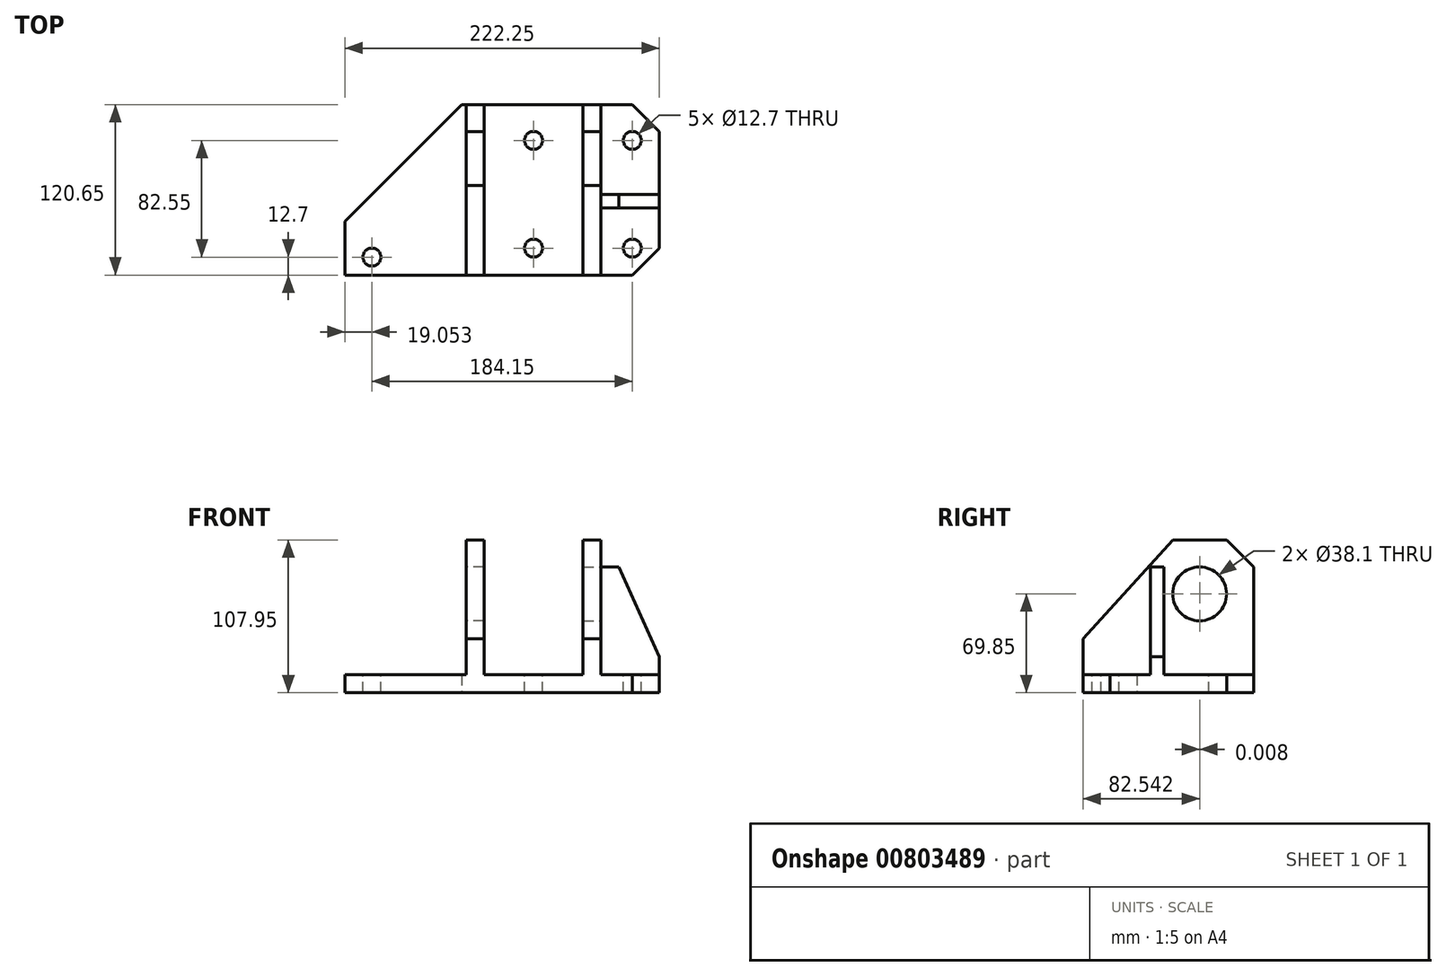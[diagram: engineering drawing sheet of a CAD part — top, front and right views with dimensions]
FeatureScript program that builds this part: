
annotation { "Feature Type Name" : "Feature", "Feature Type Description" : "" }
export const myFeature = defineFeature(function(context is Context, id is Id, definition is map)
    precondition{}
    {
        {
            var Q0;
            Q0=qCreatedBy(makeId("Top.planeOp"),FACE);
            var sketch = newSketch(context, id + "F0", { "sketchPlane" : qUnion([Q0])});
            skLineSegment(sketch, "E0", {"start": v(-62.09, -1.4) * mm, "end": v(-62.09, -39.5) * mm});
            skLineSegment(sketch, "E1", {"start": v(-62.09, -39.5) * mm, "end": v(141.11, -39.5) * mm});
            skLineSegment(sketch, "E2", {"start": v(160.16, -20.46) * mm, "end": v(160.16, 81.14) * mm});
            skLineSegment(sketch, "E3", {"start": v(160.16, -20.46) * mm, "end": v(141.11, -39.5) * mm});
            skLineSegment(sketch, "E4", {"start": v(160.16, 81.14) * mm, "end": v(71.26, 81.14) * mm});
            skLineSegment(sketch, "E5", {"start": v(71.26, 81.14) * mm, "end": v(36.34, 81.14) * mm});
            skLineSegment(sketch, "E6", {"start": v(36.34, 81.14) * mm, "end": v(20.46, 81.14) * mm});
            skLineSegment(sketch, "E7", {"start": v(20.46, 81.14) * mm, "end": v(-62.09, -1.4) * mm});
            skSolve(sketch);
        }
        {
            var Q0;
            Q0 = qSketchRegion(id + "F0", true);
            extrude(context, id + "F1", {"entities" : qUnion([Q0]), "depth" : 12.7 * mm, "offsetDistance" : 25.4 * mm});
        }
        {
            var Q0;
            Q0=makeQuery(id+"F1.opExtrude","CAP_FACE",FACE,{"disambiguationData":[OSD([sQuery(id+"F0.wireOp",EDGE,"E0"),sQuery(id+"F0.wireOp",EDGE,"E1"),sQuery(id+"F0.wireOp",EDGE,"E2"),sQuery(id+"F0.wireOp",EDGE,"E3"),sQuery(id+"F0.wireOp",EDGE,"E4"),sQuery(id+"F0.wireOp",EDGE,"E5"),sQuery(id+"F0.wireOp",EDGE,"E6"),sQuery(id+"F0.wireOp",EDGE,"E7")])],"isStart":false});
            var sketch = newSketch(context, id + "F2", { "sketchPlane" : qUnion([Q0])});
            skLineSegment(sketch, "E8", {"start": v(160.16, 81.14) * mm, "end": v(160.16, 62.1) * mm});
            skLineSegment(sketch, "E9", {"start": v(160.16, 81.14) * mm, "end": v(141.11, 81.14) * mm});
            skLineSegment(sketch, "E10", {"start": v(141.11, 81.14) * mm, "end": v(160.16, 62.1) * mm});
            skSolve(sketch);
        }
        {
            var Q0;
            Q0 = qSketchRegion(id + "F2", true);
            extrude(context, id + "F3", {"entities" : qUnion([Q0]), "operationType" : NewBodyOperationType.REMOVE, "oppositeDirection" : true, "depth" : 25.4 * mm, "offsetDistance" : 25.4 * mm});
        }
        {
            var Q0;
            Q0=makeQuery(id+"F1.opExtrude","CAP_FACE",FACE,{"disambiguationData":[OSD([sQuery(id+"F0.wireOp",EDGE,"E0"),sQuery(id+"F0.wireOp",EDGE,"E1"),sQuery(id+"F0.wireOp",EDGE,"E2"),sQuery(id+"F0.wireOp",EDGE,"E3"),sQuery(id+"F0.wireOp",EDGE,"E4"),sQuery(id+"F0.wireOp",EDGE,"E5"),sQuery(id+"F0.wireOp",EDGE,"E6"),sQuery(id+"F0.wireOp",EDGE,"E7")])],"isStart":false});
            var sketch = newSketch(context, id + "F4", { "sketchPlane" : qUnion([Q0])});
            skLineSegment(sketch, "E11", {"start": v(20.46, 81.14) * mm, "end": v(23.64, 81.14) * mm});
            skLineSegment(sketch, "E12", {"start": v(23.64, 81.14) * mm, "end": v(36.34, 81.14) * mm});
            skLineSegment(sketch, "E13", {"start": v(36.34, 81.14) * mm, "end": v(36.34, -39.5) * mm});
            skLineSegment(sketch, "E14", {"start": v(23.64, 81.14) * mm, "end": v(23.64, -39.5) * mm});
            skLineSegment(sketch, "E15", {"start": v(36.34, 81.14) * mm, "end": v(106.19, 81.14) * mm});
            skLineSegment(sketch, "E16", {"start": v(106.19, 81.14) * mm, "end": v(106.19, -39.5) * mm});
            skLineSegment(sketch, "E17", {"start": v(106.19, -39.5) * mm, "end": v(106.19, 81.14) * mm});
            skLineSegment(sketch, "E18", {"start": v(106.19, 81.14) * mm, "end": v(118.89, 81.14) * mm});
            skLineSegment(sketch, "E19", {"start": v(118.89, 81.14) * mm, "end": v(118.89, -39.5) * mm});
            skLineSegment(sketch, "E20", {"start": v(118.89, -39.5) * mm, "end": v(106.19, -39.5) * mm});
            skLineSegment(sketch, "E21", {"start": v(36.34, -39.5) * mm, "end": v(23.64, -39.5) * mm});
            skSolve(sketch);
        }
        {
            var Q0;
            Q0 = qSketchRegion(id + "F4", true);
            extrude(context, id + "F5", {"entities" : qUnion([Q0]), "operationType" : NewBodyOperationType.ADD, "depth" : 95.25 * mm, "offsetDistance" : 25.4 * mm});
        }
        {
            var Q0;
            Q0=makeQuery(id+"F5.opExtrude","SWEPT_FACE",FACE,{"disambiguationData":[OSD([sQuery(id+"F4.wireOp",EDGE,"E14")])]});
            var sketch = newSketch(context, id + "F6", { "sketchPlane" : qUnion([Q0])});
            skLineSegment(sketch, "E22", {"start": v(-81.14, 107.95) * mm, "end": v(-62.1, 107.95) * mm});
            skLineSegment(sketch, "E23", {"start": v(-81.14, 107.95) * mm, "end": v(-81.14, 88.9) * mm});
            skLineSegment(sketch, "E24", {"start": v(-81.14, 88.9) * mm, "end": v(-62.1, 107.95) * mm});
            skSolve(sketch);
        }
        {
            var Q0;
            Q0 = qSketchRegion(id + "F6", true);
            extrude(context, id + "F7", {"entities" : qUnion([Q0]), "operationType" : NewBodyOperationType.REMOVE, "oppositeDirection" : true, "depth" : 25.4 * mm, "offsetDistance" : 25.4 * mm});
        }
        {
            var Q0;
            Q0=makeQuery(id+"F5.opExtrude","SWEPT_FACE",FACE,{"disambiguationData":[OSD([sQuery(id+"F4.wireOp",EDGE,"E14")])]});
            var sketch = newSketch(context, id + "F8", { "sketchPlane" : qUnion([Q0])});
            skLineSegment(sketch, "E25", {"start": v(-62.1, 107.95) * mm, "end": v(-24, 107.95) * mm});
            skLineSegment(sketch, "E26", {"start": v(39.5, 12.7) * mm, "end": v(39.5, 38.1) * mm});
            skLineSegment(sketch, "E27", {"start": v(39.5, 38.1) * mm, "end": v(-24, 107.95) * mm});
            skSolve(sketch);
        }
        {
            var Q0;
            Q0 = qSketchRegion(id + "F8", true);
            var Q1;
            {var subQ0=sQuery(id+"F8.wireOp",EDGE,"E27");Q1=makeQuery(id+"F8.imprint","IMPRINT",FACE,{"disambiguationData":[TD([[makeQuery(id+"F8.imprint","IMPRINT",EDGE,{"derivedFrom":subQ0}),-1.0]])]});}
            extrude(context, id + "F9", {"entities" : qUnion([Q0, Q1]), "operationType" : NewBodyOperationType.REMOVE, "oppositeDirection" : true, "depth" : 25.4 * mm, "offsetDistance" : 25.4 * mm});
        }
        {
            var Q0;
            Q0=makeQuery(id+"F5.opExtrude","SWEPT_FACE",FACE,{"disambiguationData":[OSD([sQuery(id+"F4.wireOp",EDGE,"E19")])]});
            var sketch = newSketch(context, id + "F10", { "sketchPlane" : qUnion([Q0])});
            skLineSegment(sketch, "E28", {"start": v(81.14, 88.9) * mm, "end": v(81.14, 107.95) * mm});
            skLineSegment(sketch, "E29", {"start": v(81.14, 107.95) * mm, "end": v(62.1, 107.95) * mm});
            skLineSegment(sketch, "E30", {"start": v(62.1, 107.95) * mm, "end": v(81.14, 88.9) * mm});
            skLineSegment(sketch, "E31", {"start": v(62.1, 107.95) * mm, "end": v(24, 107.95) * mm});
            skLineSegment(sketch, "E32", {"start": v(-39.5, 12.7) * mm, "end": v(-39.5, 38.1) * mm});
            skLineSegment(sketch, "E33", {"start": v(-39.5, 38.1) * mm, "end": v(24, 107.95) * mm});
            skSolve(sketch);
        }
        {
            var Q0;
            {var subQ0=sQuery(id+"F10.wireOp",EDGE,"E33");Q0=makeQuery(id+"F10.imprint","IMPRINT",FACE,{"disambiguationData":[TD([[makeQuery(id+"F10.imprint","IMPRINT",EDGE,{"derivedFrom":subQ0}),1.0]])]});}
            var Q1;
            Q1=makeQuery(id+"F10.imprint","IMPRINT",FACE,{"disambiguationData":[TD([[makeQuery(id+"F10.imprint","IMPRINT",EDGE,{"derivedFrom":sQuery(id+"F10.wireOp",EDGE,"E28")}),-1.0]])]});
            extrude(context, id + "F11", {"entities" : qUnion([Q0, Q1]), "operationType" : NewBodyOperationType.REMOVE, "oppositeDirection" : true, "depth" : 25.4 * mm, "offsetDistance" : 25.4 * mm});
        }
        {
            var Q0;
            {var subQ0=sQuery(id+"F0.wireOp",EDGE,"E6");var subQ1=sQuery(id+"F0.wireOp",EDGE,"E5");var subQ2=sQuery(id+"F0.wireOp",EDGE,"E4");var subQ3=sQuery(id+"F0.wireOp",EDGE,"E3");var subQ4=sQuery(id+"F0.wireOp",EDGE,"E2");var subQ5=sQuery(id+"F0.wireOp",EDGE,"E1");Q0=makeQuery(id+"F5.boolean.opBoolean","SPLIT",FACE,{"disambiguationData":[TD([makeQuery(id+"F1.opExtrude","SWEPT_FACE",FACE,{"disambiguationData":[OSD([subQ4])]})])],"derivedFrom":makeQuery(id+"F1.opExtrude","CAP_FACE",FACE,{"disambiguationData":[OSD([sQuery(id+"F0.wireOp",EDGE,"E0"),subQ5,subQ4,subQ3,subQ2,subQ1,subQ0,sQuery(id+"F0.wireOp",EDGE,"E7")])],"isStart":false})});}
            var sketch = newSketch(context, id + "F12", { "sketchPlane" : qUnion([Q0])});
            skLineSegment(sketch, "E34", {"start": v(118.89, -39.5) * mm, "end": v(118.89, 8.12) * mm});
            skLineSegment(sketch, "E35", {"start": v(118.89, 8.12) * mm, "end": v(160.16, 8.12) * mm});
            skLineSegment(sketch, "E36", {"start": v(160.16, 8.12) * mm, "end": v(160.16, 17.64) * mm});
            skLineSegment(sketch, "E37", {"start": v(160.16, 17.64) * mm, "end": v(118.89, 17.64) * mm});
            skPoint(sketch, "E37.endSnap0", {"position": v(118.89, 20.82) * mm});
            skSolve(sketch);
        }
        {
            var Q0;
            Q0 = qSketchRegion(id + "F12", true);
            var Q1;
            {var subQ0=sQuery(id+"F12.wireOp",EDGE,"E35");Q1=makeQuery(id+"F12.imprint","IMPRINT",FACE,{"disambiguationData":[TD([[makeQuery(id+"F12.imprint","IMPRINT",EDGE,{"derivedFrom":subQ0}),1.0]])]});}
            extrude(context, id + "F13", {"entities" : qUnion([Q0, Q1]), "operationType" : NewBodyOperationType.ADD, "depth" : 76.2 * mm, "offsetDistance" : 25.4 * mm});
        }
        {
            var Q0;
            Q0=makeQuery(id+"F13.opExtrude","SWEPT_FACE",FACE,{"disambiguationData":[OSD([sQuery(id+"F12.wireOp",EDGE,"E35")])]});
            var sketch = newSketch(context, id + "F14", { "sketchPlane" : qUnion([Q0])});
            skLineSegment(sketch, "E38", {"start": v(118.89, 88.9) * mm, "end": v(131.59, 88.9) * mm});
            skLineSegment(sketch, "E39", {"start": v(160.16, 12.7) * mm, "end": v(160.16, 25.4) * mm});
            skLineSegment(sketch, "E40", {"start": v(160.16, 25.4) * mm, "end": v(131.59, 88.9) * mm});
            skSolve(sketch);
        }
        {
            var Q0;
            Q0 = qSketchRegion(id + "F14", true);
            var Q1;
            {var subQ0=sQuery(id+"F14.wireOp",EDGE,"E40");Q1=makeQuery(id+"F14.imprint","IMPRINT",FACE,{"disambiguationData":[TD([[makeQuery(id+"F14.imprint","IMPRINT",EDGE,{"derivedFrom":subQ0}),-1.0]])]});}
            extrude(context, id + "F15", {"entities" : qUnion([Q0, Q1]), "operationType" : NewBodyOperationType.REMOVE, "oppositeDirection" : true, "depth" : 25.4 * mm, "offsetDistance" : 25.4 * mm});
        }
        {
            var Q0;
            {var subQ0=sQuery(id+"F0.wireOp",EDGE,"E7");var subQ1=sQuery(id+"F0.wireOp",EDGE,"E6");var subQ2=sQuery(id+"F0.wireOp",EDGE,"E5");var subQ3=sQuery(id+"F0.wireOp",EDGE,"E4");var subQ4=sQuery(id+"F0.wireOp",EDGE,"E1");var subQ5=sQuery(id+"F0.wireOp",EDGE,"E0");Q0=makeQuery(id+"F5.boolean.opBoolean","SPLIT",FACE,{"disambiguationData":[TD([makeQuery(id+"F1.opExtrude","SWEPT_FACE",FACE,{"disambiguationData":[OSD([subQ5])]})])],"derivedFrom":makeQuery(id+"F1.opExtrude","CAP_FACE",FACE,{"disambiguationData":[OSD([subQ5,subQ4,sQuery(id+"F0.wireOp",EDGE,"E2"),sQuery(id+"F0.wireOp",EDGE,"E3"),subQ3,subQ2,subQ1,subQ0])],"isStart":false})});}
            var sketch = newSketch(context, id + "F16", { "sketchPlane" : qUnion([Q0])});
            skLineSegment(sketch, "E41", {"start": v(-62.09, -39.5) * mm, "end": v(-43.04, -39.5) * mm});
            skLineSegment(sketch, "E42", {"start": v(-62.09, -39.5) * mm, "end": v(-62.09, -26.8) * mm});
            skLineSegment(sketch, "E43", {"start": v(-62.09, -26.8) * mm, "end": v(-43.04, -26.8) * mm});
            skCircle(sketch, "E44", {"center": v(-43.04, -26.8) * mm, "radius": 6.35 * mm});
            skSolve(sketch);
        }
        {
            var Q0;
            Q0 = qSketchRegion(id + "F16", true);
            extrude(context, id + "F17", {"entities" : qUnion([Q0]), "operationType" : NewBodyOperationType.REMOVE, "oppositeDirection" : true, "depth" : 25.4 * mm, "offsetDistance" : 25.4 * mm});
        }
        {
            var Q0;
            {var subQ1=sQuery(id+"F0.wireOp",EDGE,"E2");var subQ2=makeQuery(id+"F1.opExtrude","SWEPT_FACE",FACE,{"disambiguationData":[OSD([subQ1])]});var subQ3=sQuery(id+"F0.wireOp",EDGE,"E3");var subQ6=sQuery(id+"F0.wireOp",EDGE,"E1");var subQ7=makeQuery(id+"F1.opExtrude","SWEPT_FACE",FACE,{"disambiguationData":[OSD([subQ6])]});var subQ9=sQuery(id+"F0.wireOp",EDGE,"E6");var subQ10=sQuery(id+"F0.wireOp",EDGE,"E5");var subQ11=sQuery(id+"F0.wireOp",EDGE,"E4");Q0=makeQuery(id+"F13.boolean.opBoolean","SPLIT",FACE,{"disambiguationData":[TD([subQ7])],"derivedFrom":makeQuery(id+"F5.boolean.opBoolean","SPLIT",FACE,{"disambiguationData":[TD([subQ2])],"derivedFrom":makeQuery(id+"F1.opExtrude","CAP_FACE",FACE,{"disambiguationData":[OSD([sQuery(id+"F0.wireOp",EDGE,"E0"),subQ6,subQ1,subQ3,subQ11,subQ10,subQ9,sQuery(id+"F0.wireOp",EDGE,"E7")])],"isStart":false})})});}
            var sketch = newSketch(context, id + "F18", { "sketchPlane" : qUnion([Q0])});
            skLineSegment(sketch, "E45", {"start": v(141.11, -39.5) * mm, "end": v(141.11, -20.46) * mm});
            skCircle(sketch, "E46", {"center": v(141.11, -20.46) * mm, "radius": 6.35 * mm});
            skSolve(sketch);
        }
        {
            var Q0;
            Q0 = qSketchRegion(id + "F18", true);
            extrude(context, id + "F19", {"entities" : qUnion([Q0]), "operationType" : NewBodyOperationType.REMOVE, "oppositeDirection" : true, "depth" : 25.4 * mm, "offsetDistance" : 25.4 * mm});
        }
        {
            var Q0;
            {var subQ1=sQuery(id+"F0.wireOp",EDGE,"E6");var subQ2=sQuery(id+"F0.wireOp",EDGE,"E5");var subQ3=sQuery(id+"F0.wireOp",EDGE,"E4");var subQ5=makeQuery(id+"F3.boolean.opBoolean","COPY",FACE,{"derivedFrom":makeQuery(id+"F3.opExtrude","SWEPT_FACE",FACE,{"disambiguationData":[OSD([sQuery(id+"F2.wireOp",EDGE,"E10")])]})});var subQ6=sQuery(id+"F0.wireOp",EDGE,"E2");var subQ7=makeQuery(id+"F1.opExtrude","SWEPT_FACE",FACE,{"disambiguationData":[OSD([subQ6])]});var subQ10=sQuery(id+"F0.wireOp",EDGE,"E3");var subQ11=sQuery(id+"F0.wireOp",EDGE,"E1");Q0=makeQuery(id+"F13.boolean.opBoolean","SPLIT",FACE,{"disambiguationData":[TD([subQ5])],"derivedFrom":makeQuery(id+"F5.boolean.opBoolean","SPLIT",FACE,{"disambiguationData":[TD([subQ7])],"derivedFrom":makeQuery(id+"F1.opExtrude","CAP_FACE",FACE,{"disambiguationData":[OSD([sQuery(id+"F0.wireOp",EDGE,"E0"),subQ11,subQ6,subQ10,subQ3,subQ2,subQ1,sQuery(id+"F0.wireOp",EDGE,"E7")])],"isStart":false})})});}
            var sketch = newSketch(context, id + "F20", { "sketchPlane" : qUnion([Q0])});
            skLineSegment(sketch, "E47", {"start": v(141.11, 81.14) * mm, "end": v(141.11, 55.74) * mm});
            skCircle(sketch, "E48", {"center": v(141.11, 55.74) * mm, "radius": 6.35 * mm});
            skSolve(sketch);
        }
        {
            var Q0;
            Q0=makeQuery(id+"F20.imprint","IMPRINT",FACE,{"disambiguationData":[TD([[makeQuery(id+"F20.imprint","IMPRINT",EDGE,{"derivedFrom":sQuery(id+"F20.wireOp",EDGE,"E48")}),1.0]])]});
            extrude(context, id + "F21", {"entities" : qUnion([Q0]), "operationType" : NewBodyOperationType.REMOVE, "oppositeDirection" : true, "depth" : 25.4 * mm, "offsetDistance" : 25.4 * mm});
        }
        {
            var Q0;
            {var subQ0=sQuery(id+"F0.wireOp",EDGE,"E6");var subQ1=sQuery(id+"F0.wireOp",EDGE,"E5");var subQ2=sQuery(id+"F0.wireOp",EDGE,"E4");var subQ3=sQuery(id+"F0.wireOp",EDGE,"E1");Q0=makeQuery(id+"F5.boolean.opBoolean","SPLIT",FACE,{"disambiguationData":[TD([makeQuery(id+"F5.opExtrude","SWEPT_FACE",FACE,{"disambiguationData":[OSD([sQuery(id+"F4.wireOp",EDGE,"E13")])]})])],"derivedFrom":makeQuery(id+"F1.opExtrude","CAP_FACE",FACE,{"disambiguationData":[OSD([sQuery(id+"F0.wireOp",EDGE,"E0"),subQ3,sQuery(id+"F0.wireOp",EDGE,"E2"),sQuery(id+"F0.wireOp",EDGE,"E3"),subQ2,subQ1,subQ0,sQuery(id+"F0.wireOp",EDGE,"E7")])],"isStart":false})});}
            var sketch = newSketch(context, id + "F22", { "sketchPlane" : qUnion([Q0])});
            skLineSegment(sketch, "E49", {"start": v(36.34, -39.5) * mm, "end": v(71.26, -39.5) * mm});
            skLineSegment(sketch, "E50", {"start": v(71.26, -39.5) * mm, "end": v(71.26, -20.46) * mm});
            skLineSegment(sketch, "E51", {"start": v(71.26, -20.46) * mm, "end": v(71.26, 55.74) * mm});
            skCircle(sketch, "E52", {"center": v(71.26, 55.74) * mm, "radius": 6.35 * mm});
            skCircle(sketch, "E53", {"center": v(71.26, -20.46) * mm, "radius": 6.35 * mm});
            skSolve(sketch);
        }
        {
            var Q0;
            Q0 = qSketchRegion(id + "F22", true);
            extrude(context, id + "F23", {"entities" : qUnion([Q0]), "operationType" : NewBodyOperationType.REMOVE, "oppositeDirection" : true, "depth" : 25.4 * mm, "offsetDistance" : 25.4 * mm});
        }
        {
            var Q0;
            Q0=makeQuery(id+"F5.opExtrude","SWEPT_FACE",FACE,{"disambiguationData":[OSD([sQuery(id+"F4.wireOp",EDGE,"E19")])]});
            var sketch = newSketch(context, id + "F24", { "sketchPlane" : qUnion([Q0])});
            skLineSegment(sketch, "E54", {"start": v(81.14, 88.9) * mm, "end": v(81.14, 69.85) * mm});
            skLineSegment(sketch, "E55", {"start": v(81.14, 69.85) * mm, "end": v(43.03, 69.85) * mm});
            skCircle(sketch, "E56", {"center": v(43.03, 69.85) * mm, "radius": 19.05 * mm});
            skSolve(sketch);
        }
        {
            var Q0;
            Q0 = qSketchRegion(id + "F24", true);
            extrude(context, id + "F25", {"entities" : qUnion([Q0]), "operationType" : NewBodyOperationType.REMOVE, "oppositeDirection" : true, "depth" : 25.4 * mm, "offsetDistance" : 25.4 * mm});
        }
        {
            var Q0;
            Q0=makeQuery(id+"F5.opExtrude","SWEPT_FACE",FACE,{"disambiguationData":[OSD([sQuery(id+"F4.wireOp",EDGE,"E14")])]});
            var sketch = newSketch(context, id + "F26", { "sketchPlane" : qUnion([Q0])});
            skLineSegment(sketch, "E57", {"start": v(-81.14, 88.9) * mm, "end": v(-81.14, 69.85) * mm});
            skLineSegment(sketch, "E58", {"start": v(-81.14, 69.85) * mm, "end": v(-43.04, 69.85) * mm});
            skCircle(sketch, "E59", {"center": v(-43.04, 69.85) * mm, "radius": 19.05 * mm});
            skSolve(sketch);
        }
        {
            var Q0;
            Q0 = qSketchRegion(id + "F26", true);
            extrude(context, id + "F27", {"entities" : qUnion([Q0]), "operationType" : NewBodyOperationType.REMOVE, "oppositeDirection" : true, "depth" : 25.4 * mm, "offsetDistance" : 25.4 * mm});
        }
    });
